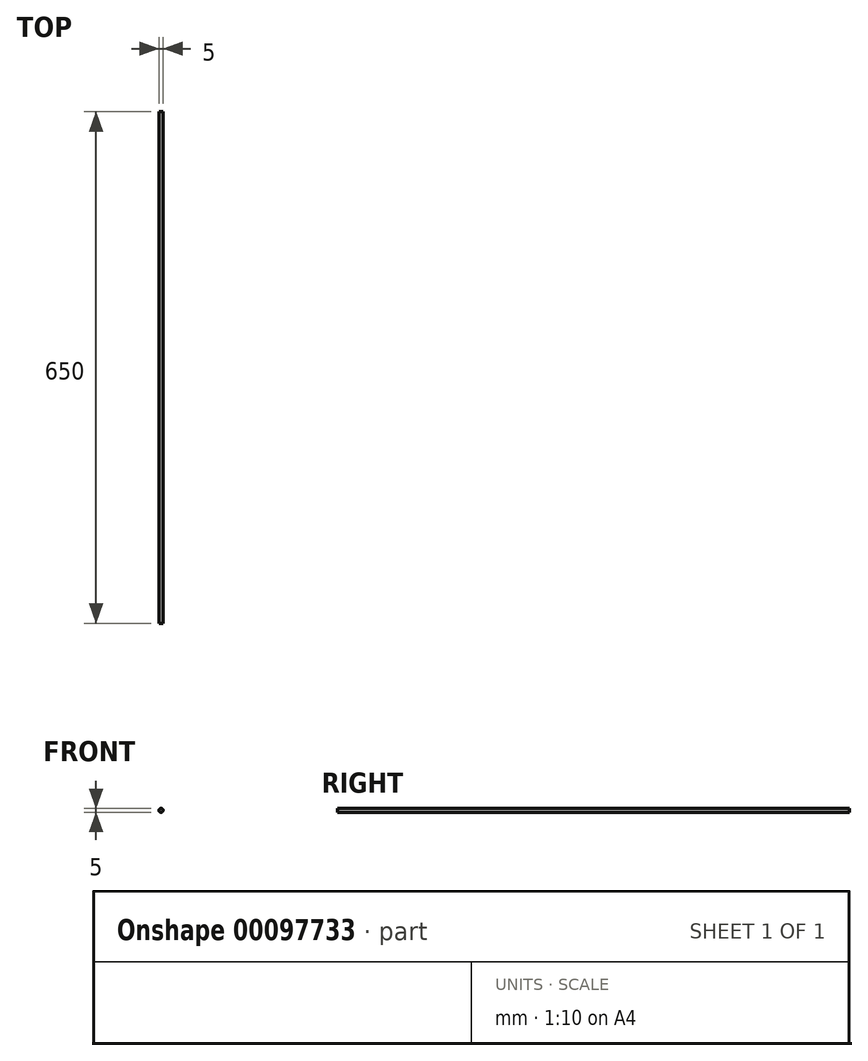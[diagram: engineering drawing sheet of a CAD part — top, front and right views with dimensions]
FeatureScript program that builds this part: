
annotation { "Feature Type Name" : "Feature", "Feature Type Description" : "" }
export const myFeature = defineFeature(function(context is Context, id is Id, definition is map)
    precondition{}
    {
        {
            var Q0;
            Q0=qCreatedBy(makeId("Front.planeOp"),FACE);
            var sketch = newSketch(context, id + "F0", { "sketchPlane" : qUnion([Q0])});
            skCircle(sketch, "E0", {"center": v(0, 0) * mm, "radius": 2.5 * mm});
            skSolve(sketch);
        }
        {
            var Q0;
            Q0=makeQuery(id+"F0.imprint","IMPRINT",FACE,{"disambiguationData":[TD([[makeQuery(id+"F0.imprint","IMPRINT",EDGE,{"derivedFrom":sQuery(id+"F0.wireOp",EDGE,"E0")}),1.0]])]});
            extrude(context, id + "F1", {"entities" : qUnion([Q0]), "endBound" : BoundingType.SYMMETRIC, "depth" : 650 * mm});
        }
    });
